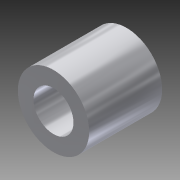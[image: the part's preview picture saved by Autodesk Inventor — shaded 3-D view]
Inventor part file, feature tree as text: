
AUTODESK INVENTOR PART (.ipt)
format: ipt  version: 2015 (Build 190159000, 159)  size: 89,088 bytes
history: native  units: in
note: dims shown in document units (in); Inventor stores cm internally (conversion verified against a paired STEP export)
features: extrude x1, sketch x1
ambient origin geometry x8: Origin, YZ Plane, XZ Plane, XY Plane, X Axis, Y Axis, Z Axis, Center Point
bodies: Solid1 (feature_tree)
feature tree (2):
  extrude  "Extrusion1"  Depth=0.256in
  sketch  "Sketch1"  dims[d0=0.14in d1=0.25in d2=0.256in d3=0.0in]
